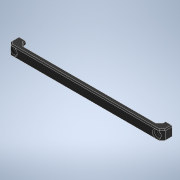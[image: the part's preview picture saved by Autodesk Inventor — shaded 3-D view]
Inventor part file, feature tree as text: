
AUTODESK INVENTOR PART (.ipt)
format: ipt  version: 2021 (Build 250183000, 183)  size: 536,576 bytes
history: native  units: mm
features: extrude x7, sketch x7, chamfer x7, plane x3, thicken_offset x2, mirror x1, projected_geometry x1
ambient origin geometry x8: Origin, YZ Plane, XZ Plane, XY Plane, X Axis, Y Axis, Z Axis, Center Point
bodies: Solid1 (feature_tree)
feature tree (28):
  extrude  "Extrusion1"  Depth=10.0mm
  extrude  "Extrusion2"  Depth=67.5mm
  extrude  "Extrusion3"  Depth=5.0mm
  sketch  "Sketch4"  dims[d10=0.0mm d11=0.0mm d12=1.6mm]
  plane  "Work Plane1"
  extrude  "Extrusion5"  Depth=1.6mm
  extrude  "Extrusion6"  Depth=6.0mm
  sketch  "Sketch6"  dims[d21=2.0mm d22=3.75mm d23=0.0mm d25=5.5mm d27=0.0mm d28=0.0mm]
  plane  "Work Plane2"
  extrude  "Extrusion7"  Depth=5.5mm
  mirror  "Mirror1"
  chamfer  "Chamfer3"  [1 undecoded]
  chamfer  "Chamfer5"  Distance=3.75mm
  chamfer  "Chamfer6"  Distance=2.0mm
  extrude  "Extrusion8"  Depth=3.0mm
  chamfer  "Chamfer7"  Distance=3.0mm
  chamfer  "Chamfer8"  Distance=6.0mm
  thicken_offset  "Thicken1"
  thicken_offset  "Thicken2"
  chamfer  "Chamfer9"  Distance=1.0mm Angle=45.0deg
  chamfer  "Chamfer10"  Distance=1.0mm Angle=45.0deg
  sketch  "Sketch1"  dims[d0=150.0mm d1=10.0mm]
  sketch  "Sketch2"  dims[d2=10.0mm d3=0.0mm d7=67.5mm]
  sketch  "Sketch3"  dims[d8=135.0mm d9=5.0mm]
  sketch  "Sketch5"  dims[d13=2.0mm d14=0.0mm d18=6.0mm]
  projected_geometry  "Projected Loop1"
  plane  "Work Plane3"
  sketch  "Sketch7"  dims[d29=-2.0mm d30=3.75mm d31=0.0mm d32=2.0mm d33=3.0mm d34=3.0mm d35=6.0mm d39=1.0mm d40=2.0mm d41=45.0deg d45=1.0mm d46=2.0mm d47=45.0deg d48=70.0mm d49=3.0mm d50=2.0mm d51=45.0deg d52=0.0mm d53=0.0mm d54=1.0mm d55=2.0mm d56=45.0deg d57=0.5mm d58=2.0mm d59=45.0deg d60=0.1mm d61=0.2mm d62=0.1mm d63=0.2mm d64=3.0mm d65=2.0mm d66=45.0deg d67=1.0mm d68=2.0mm d69=45.0deg d70=6.5mm]
note: 1 required parameter value undecoded (feature->parameter linkage not recoverable at this tier; creation-order binding heuristic only, values carry confidence <= 0.55)
